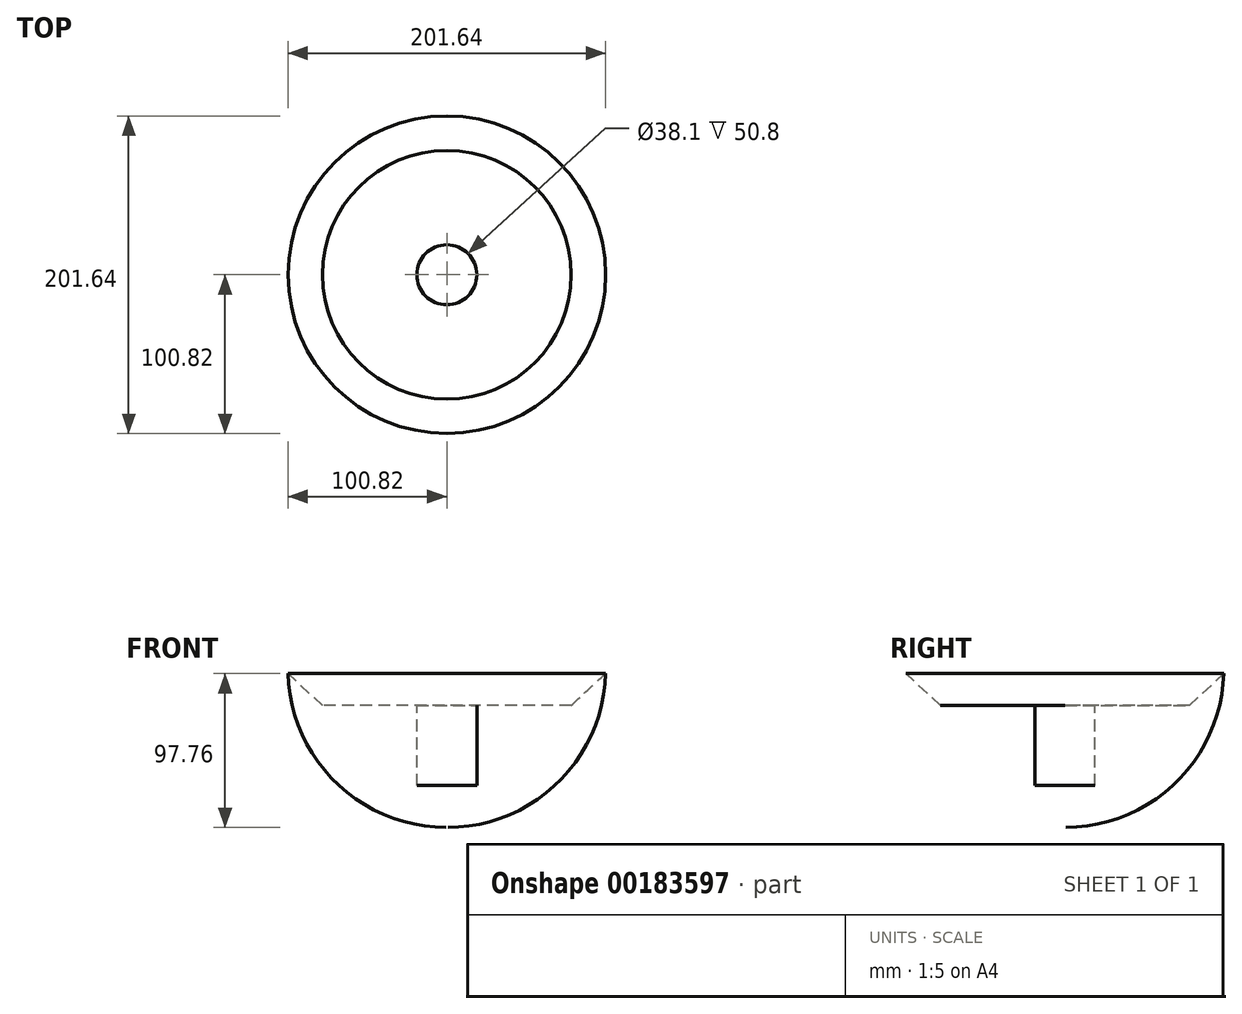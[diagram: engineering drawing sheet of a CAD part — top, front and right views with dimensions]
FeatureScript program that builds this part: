
annotation { "Feature Type Name" : "Feature", "Feature Type Description" : "" }
export const myFeature = defineFeature(function(context is Context, id is Id, definition is map)
    precondition{}
    {
        {
            var Q0;
            Q0=qCreatedBy(makeId("Front.planeOp"),FACE);
            var sketch = newSketch(context, id + "F0", { "sketchPlane" : qUnion([Q0])});
            skLineSegment(sketch, "E0", {"start": v(0, 103.32) * mm, "end": v(0, -20.32) * mm});
            skArc(sketch, "E1", {"start": v(100.82, 0) * mm, "mid": v(72.28, 73) * mm, "end": v(0, 103.32) * mm});
            skLineSegment(sketch, "E2", {"start": v(-108.8, 0) * mm, "end": v(100.82, 0) * mm, "construction": true});
            skLineSegment(sketch, "E3", {"start": v(-109.26, -20.32) * mm, "end": v(78.96, -20.32) * mm, "construction": true});
            skLineSegment(sketch, "E4", {"start": v(100.82, 0) * mm, "end": v(78.96, -20.32) * mm, "construction": true});
            skLineSegment(sketch, "E5", {"start": v(0, 0) * mm, "end": v(100.82, 0) * mm});
            skLineSegment(sketch, "E6", {"start": v(78.96, -20.32) * mm, "end": v(100.82, 0) * mm});
            skLineSegment(sketch, "E7", {"start": v(78.96, -20.32) * mm, "end": v(0, -20.32) * mm});
            skSolve(sketch);
        }
        {
            var Q0;
            {var subQ0=sQuery(id+"F0.wireOp",EDGE,"E1");Q0=makeQuery(id+"F0.imprint","IMPRINT",FACE,{"disambiguationData":[TD([[makeQuery(id+"F0.imprint","IMPRINT",EDGE,{"derivedFrom":subQ0}),1.0]])]});}
            var Q1;
            {var subQ2=sQuery(id+"F0.wireOp",EDGE,"E5");Q1=makeQuery(id+"F0.imprint","IMPRINT",FACE,{"disambiguationData":[TD([[makeQuery(id+"F0.imprint","IMPRINT",EDGE,{"derivedFrom":subQ2}),-1.0]])]});}
            var Q2;
            Q2=sQuery(id+"F0.wireOp",EDGE,"E0");
            revolve(context, id + "F1", {"entities" : qUnion([Q0, Q1]), "axis" : qUnion([Q2]), "revolveType" : RevolveType.FULL});
        }
        {
            var Q0;
            Q0=makeQuery(id+"F1.opRevolve","SWEPT_FACE",FACE,{"disambiguationData":[OSD([sQuery(id+"F0.wireOp",EDGE,"E7")])]});
            var sketch = newSketch(context, id + "F2", { "sketchPlane" : qUnion([Q0])});
            skCircle(sketch, "E8", {"center": v(0, 0) * mm, "radius": 19.05 * mm});
            skSolve(sketch);
        }
        {
            var Q0;
            Q0=makeQuery(id+"F2.imprint","IMPRINT",FACE,{"disambiguationData":[TD([[makeQuery(id+"F2.imprint","IMPRINT",EDGE,{"derivedFrom":sQuery(id+"F2.wireOp",EDGE,"E8")}),1.0]])]});
            extrude(context, id + "F3", {"entities" : qUnion([Q0]), "operationType" : NewBodyOperationType.ADD, "depth" : 50.8 * mm});
        }
    });
